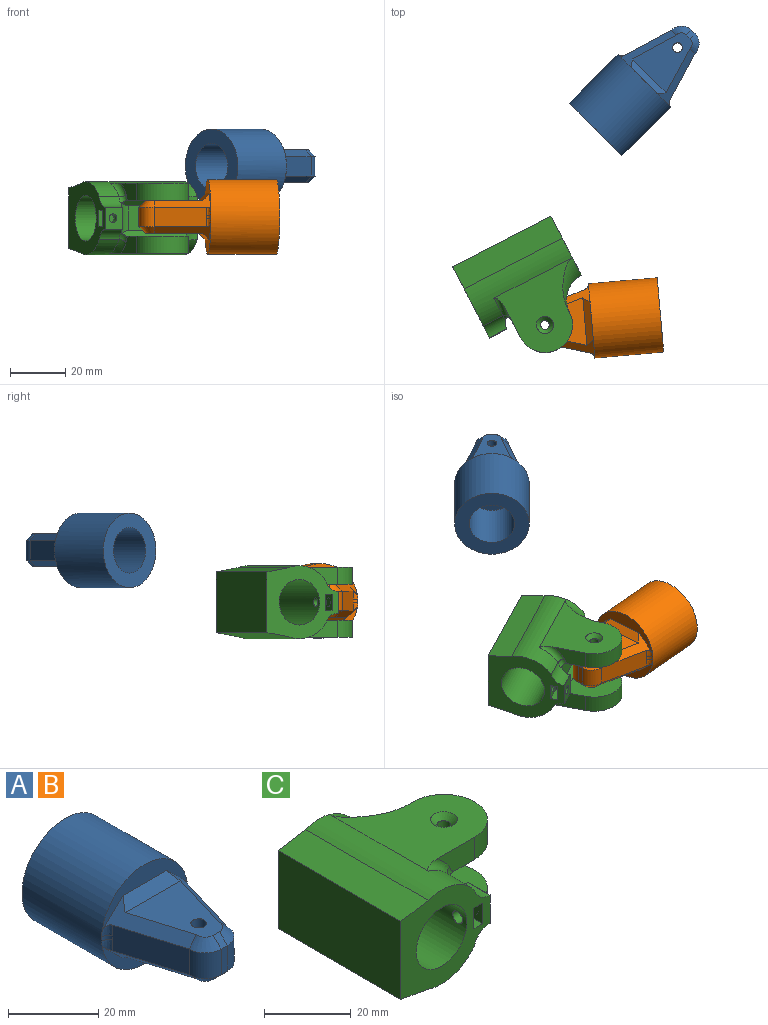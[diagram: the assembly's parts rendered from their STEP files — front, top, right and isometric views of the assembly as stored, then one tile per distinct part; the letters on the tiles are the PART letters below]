
ASSEMBLY  parts=3 mates=1
PART A: 34 faces, bbox 27.6x50.6x27.6 mm
  f0: plane 1.14x0.01mm, normal (0,-1,0), area 0mm2, adj f11,f29
  f1: plane 26.62x11.26mm, normal (0,-1,0), area 100.3mm2, adj f11,f16,f20,f26
  f2: plane 1.14x0.01mm, normal (0,-1,0), area 0mm2, adj f11,f32
  f3: plane 20x17.28mm, normal (0,0,1), area 215.8mm2, adj f6,f16,f17,f18,f19,f20,f26
  f4: plane 20x17.28mm, normal (0,0,-1), area 215.8mm2, adj f6,f21,f22,f23,f24,f25,f27
  f5: plane 7x2mm, normal (0,-1,0), area 14mm2, adj f7,f8,f18,f25
  f6: cylinder r=1.75mm len=12mm, axis (0,0,1), area 131.9mm2, adj f3,f4
  f7: cylinder r=5mm len=7mm, axis (0,0,1), area 55mm2, adj f5,f14,f17,f24
  f8: cylinder r=5mm len=7mm, axis (0,0,-1), area 55mm2, adj f5,f15,f19,f23
  f9: plane 26.62x11.26mm, normal (0,-1,0), area 100.3mm2, adj f11,f21,f22,f27
  f10: cylinder r=8.25mm len=20mm, axis (0,-1,0), area 1036.7mm2, adj f12,f13
  f11: cylinder r=13.5mm len=27mm, axis (0,-1,0), area 2120.6mm2, adj f0,f1,f2,f9,f12,f28,f30,f31
  f12: plane 27x27mm, normal (0,1,0), area 358.7mm2, adj f10,f11
  f13: plane 16.5x16.5mm, normal (0,1,0), area 213.8mm2, adj f10
  f14: plane 18.63x7mm, normal (-0.96,-0.29,0), area 135.8mm2, adj f7,f16,f22,f28,f29,f30
  f15: plane 18.63x7mm, normal (0.96,-0.29,0), area 135.8mm2, adj f8,f20,f21,f31,f32,f33
  f16: plane 20.62x10.45mm, normal (-0.68,-0.2,0.71), area 78.4mm2, adj f1,f3,f14,f17,f26,f28
  f17: cone r=2.5mm half-angle=45deg, axis (0,0,-1), area 21.5mm2, adj f3,f7,f16,f18
  f18: plane 2.5x2.5mm, normal (0,-0.71,0.71), area 7.1mm2, adj f3,f5,f17,f19
  f19: cone r=2.5mm half-angle=45deg, axis (0,0,-1), area 21.5mm2, adj f3,f8,f18,f20
  f20: plane 20.62x10.45mm, normal (0.68,-0.2,0.71), area 78.4mm2, adj f1,f3,f15,f19,f26,f33
  f21: plane 20.62x10.45mm, normal (0.68,-0.2,-0.71), area 78.4mm2, adj f4,f9,f15,f23,f27,f31
  f22: plane 20.62x10.45mm, normal (-0.68,-0.2,-0.71), area 78.4mm2, adj f4,f9,f14,f24,f27,f30
  f23: cone r=2.5mm half-angle=45deg, axis (0,0,1), area 21.5mm2, adj f4,f8,f21,f25
  f24: cone r=2.5mm half-angle=45deg, axis (0,0,1), area 21.5mm2, adj f4,f7,f22,f25
  f25: plane 2.5x2.5mm, normal (0,-0.71,-0.71), area 7.1mm2, adj f4,f5,f23,f24
  f26: plane 17.28x2.5mm, normal (0,-0.71,0.71), area 54.5mm2, adj f1,f3,f16,f20
  f27: plane 17.28x2.5mm, normal (0,-0.71,-0.71), area 54.5mm2, adj f4,f9,f21,f22
  f28: bspline ~4.61x1.93mm, area 5.6mm2, adj f11,f14,f16,f29
  f29: cylinder r=2mm len=1.92mm, axis (0,0,-1), area 2.9mm2, adj f0,f14,f28,f30
  f30: bspline ~4.68x1.93mm, area 5.6mm2, adj f11,f14,f22,f29
  f31: bspline ~2.93x1.92mm, area 5.6mm2, adj f11,f15,f21,f32
  f32: cylinder r=2mm len=1.92mm, axis (0,0,-1), area 2.9mm2, adj f2,f15,f31,f33
  f33: bspline ~2.93x1.92mm, area 5.6mm2, adj f11,f15,f20,f32
PART B: same geometry as A
PART C: 51 faces, bbox 44.1x47.2x55.9 mm
  f0: plane 5.8x2.8mm, normal (0,-1,0), area 16.2mm2, adj f1,f38,f39,f50
  f1: plane 6x2.8mm, normal (0,0,1), area 16.8mm2, adj f0,f3,f38,f50
  f2: cylinder r=13.25mm len=40mm, axis (0,1,0), area 395.9mm2, adj f3,f8,f12,f35,f44,f46
  f3: plane 29x26.5mm, normal (0,-1,0), area 391.2mm2, adj f1,f2,f7,f9,f32,f33,f34,f35
  f4: plane 32x27.13mm, normal (0,0,-1), area 513.9mm2, adj f7,f13,f14,f20,f21,f27,f28,f29
  f5: cylinder r=1.6mm len=4.25mm, axis (0,0,1), area 42.7mm2, adj f16,f31
  f6: plane 28x9mm, normal (1,0,0), area 252mm2, adj f8,f18,f19,f37
  f7: cylinder r=13.25mm len=40mm, axis (0,1,0), area 395.9mm2, adj f3,f4,f8,f36,f42,f48
  f8: plane 26.5x24mm, normal (0,1,0), area 358mm2, adj f2,f6,f7,f9,f21,f22,f24,f25
  f9: cylinder r=8.25mm len=40mm, axis (0,1,0), area 2065.4mm2, adj f3,f8,f41
  f10: plane 12.38x6.25mm, normal (0,-1,0), area 57.6mm2, adj f12,f15,f23,f44,f45
  f11: plane 2.26x1.31mm, normal (0,1,0), area 1.4mm2, adj f12,f23,f24
  f12: plane 32x27.13mm, normal (0,0,1), area 516.2mm2, adj f2,f10,f11,f23,f24,f26,f44
  f13: plane 12.38x6.25mm, normal (0,-1,0), area 57.6mm2, adj f4,f16,f20,f42,f43
  f14: plane 2.26x1.31mm, normal (0,1,0), area 1.4mm2, adj f4,f20,f21
  f15: plane 24.29x18.13mm, normal (0,0,-1), area 318.7mm2, adj f10,f17,f19,f23,f25,f45
  f16: plane 24.29x18.13mm, normal (0,0,1), area 318.7mm2, adj f5,f13,f18,f20,f22,f43
  f17: cylinder r=1.6mm len=4.75mm, axis (0,0,1), area 47.7mm2, adj f15,f26
  f18: plane 32.04x2.04mm, normal (0.71,0,0.71), area 74.4mm2, adj f6,f16,f22,f36,f37,f43
  f19: plane 32.04x2.04mm, normal (0.71,0,-0.71), area 74.4mm2, adj f6,f15,f25,f35,f37,f45
  f20: cylinder r=10mm len=20mm, axis (0,0,-1), area 196.2mm2, adj f4,f13,f14,f16,f22
  f21: torus R=23.25mm, axis (0,-1,0), area 89.7mm2, adj f4,f8,f14,f22
  f22: cylinder r=10mm len=10mm, axis (0,0,-1), area 44.6mm2, adj f8,f16,f18,f20,f21
  f23: cylinder r=10mm len=20mm, axis (0,0,-1), area 196.2mm2, adj f10,f11,f12,f15,f25
  f24: torus R=23.25mm, axis (0,1,0), area 89.7mm2, adj f8,f11,f12,f25
  f25: cylinder r=10mm len=10mm, axis (0,0,-1), area 44.6mm2, adj f8,f15,f19,f23,f24
  f26: cone r=1.6mm half-angle=45deg, axis (0,0,1), area 31.3mm2, adj f12,f17
  f27: plane 5.7x2mm, normal (1,0,0), area 11.4mm2, adj f4,f28,f30,f31
  f28: plane 5.7x2mm, normal (0,-1,0), area 11.4mm2, adj f4,f27,f29,f31
  f29: plane 5.7x2mm, normal (-1,0,0), area 11.4mm2, adj f4,f28,f30,f31
  f30: plane 5.7x2mm, normal (0,1,0), area 11.4mm2, adj f4,f27,f29,f31
  f31: plane 5.7x5.7mm, normal (0,0,-1), area 24.4mm2, adj f5,f27,f28,f29,f30
  f32: plane 7x0.16mm, normal (0,0,-1), area 1.1mm2, adj f3,f34,f36,f37
  f33: plane 7x0.16mm, normal (0,0,1), area 1.1mm2, adj f3,f34,f35,f37
  f34: plane 8x7mm, normal (1,0,0), area 48mm2, adj f3,f32,f33,f37,f40
  f35: cylinder r=5mm len=8.82mm, axis (0,1,0), area 51.2mm2, adj f2,f3,f19,f33,f37,f45
  f36: cylinder r=5mm len=8.82mm, axis (0,1,0), area 51.2mm2, adj f3,f7,f18,f32,f37,f43
  f37: cylinder r=5mm len=11.28mm, axis (0,0,1), area 73.7mm2, adj f6,f18,f19,f32,f33,f34,f35,f36
  f38: plane 6x5.8mm, normal (1,0,0), area 26.8mm2, adj f0,f1,f3,f39,f41
  f39: plane 6x2.8mm, normal (0,0,-1), area 16.8mm2, adj f0,f3,f38,f50
  f40: cylinder r=1.6mm len=3.2mm, axis (1,0,0), area 22.6mm2, adj f34,f49
  f41: cylinder r=1.6mm len=3.2mm, axis (1,0,0), area 23.4mm2, adj f9,f38
  f42: torus R=15.25mm, axis (0,-1,0), area 24.1mm2, adj f4,f7,f13,f43
  f43: torus R=3mm, axis (0,-1,0), area 7.1mm2, adj f13,f16,f18,f36,f42
  f44: torus R=15.25mm, axis (0,1,0), area 24.1mm2, adj f2,f10,f12,f45
  f45: torus R=3mm, axis (0,1,0), area 7.1mm2, adj f10,f15,f19,f35,f44
  f46: plane 40x8.88mm, normal (-0.17,0,0.99), area 360.1mm2, adj f2,f3,f8,f47
  f47: plane 40x22mm, normal (-1,0,0), area 880mm2, adj f3,f8,f46,f48
  f48: plane 40x8.88mm, normal (-0.17,0,-0.99), area 360.1mm2, adj f3,f7,f8,f47
  f49: plane 3.2x3.2mm, normal (1,0,0), area 8mm2, adj f40
  f50: plane 6x5.8mm, normal (-1,0,0), area 34.8mm2, adj f0,f1,f3,f39
PLACE A rot(axis=(0,0,1),135deg) t=(-39.16,140.39,7.61)mm
PLACE B rot(axis=(0,0,-1),85deg) t=(-9.81,-50.48,-10.71)mm
PLACE C rot(axis=(0,0,-1),62.7deg) t=(-23.82,36.39,-11.21)mm
MATE cylindrical C.f5 <-> B.f6  axis (0,0,1) through (-32.06,8.77,-4.71)mm
